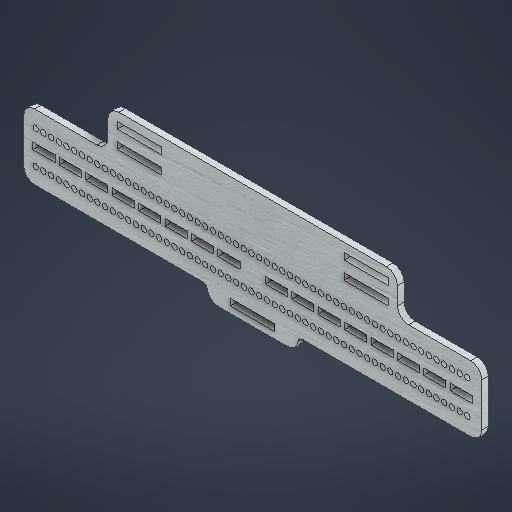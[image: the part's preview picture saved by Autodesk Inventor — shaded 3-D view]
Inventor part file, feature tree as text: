
AUTODESK INVENTOR PART (.ipt)
format: ipt  version: 2025.3 (Build 293356030, 356C)  size: 599,552 bytes
history: native  units: mm
features: other x4, sketch x3, extrude x2
ambient origin geometry x8: Origin, YZ Plane, XZ Plane, XY Plane, X Axis, Y Axis, Z Axis, Center Point
bodies: Body1 (feature_tree)
feature tree (9):
  other  "實體1"
  extrude  "擠出1"  Depth=20.0mm
  extrude  "擠出2"  Depth=3.0mm
  sketch  "草圖3"
  sketch  "草圖1"
  other  "草圖 - 矩形陣列1"
  sketch  "草圖2"
  other  "草圖 - 矩形陣列2"
  other  "草圖 - 矩形陣列3"
